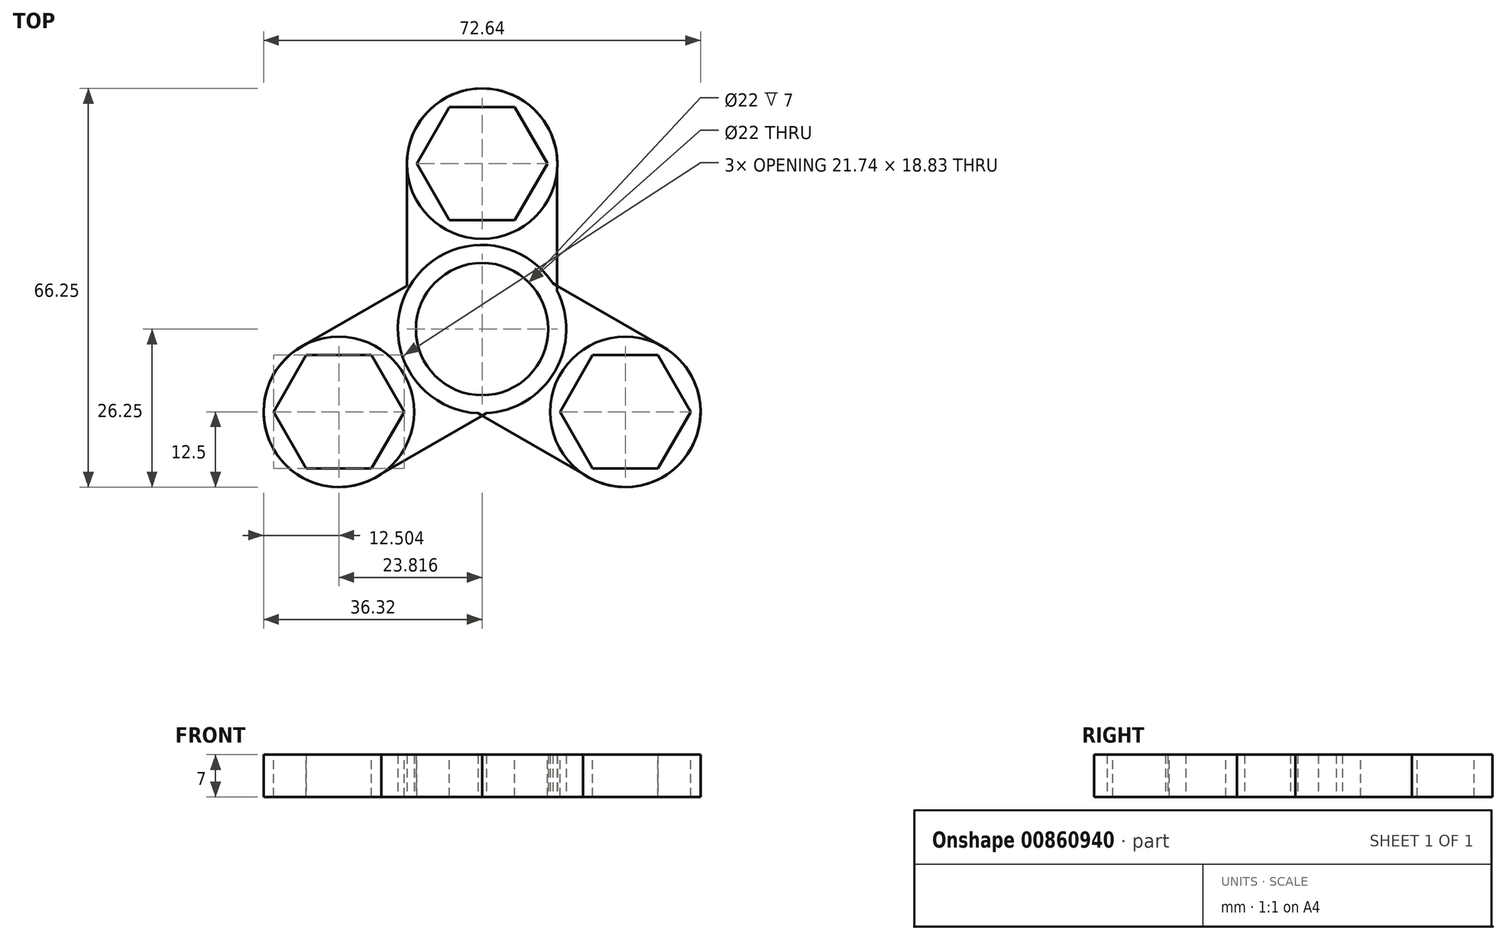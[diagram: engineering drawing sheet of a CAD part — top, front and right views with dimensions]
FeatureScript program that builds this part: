
annotation { "Feature Type Name" : "Feature", "Feature Type Description" : "" }
export const myFeature = defineFeature(function(context is Context, id is Id, definition is map)
    precondition{}
    {
        {
            var Q0;
            Q0=qCreatedBy(makeId("Top.planeOp"),FACE);
            var sketch = newSketch(context, id + "F0", { "sketchPlane" : qUnion([Q0])});
            skCircle(sketch, "E0", {"center": v(0, 0) * mm, "radius": 11 * mm});
            skCircle(sketch, "E1.0", {"center": v(0, 0) * mm, "radius": 14 * mm});
            skCircle(sketch, "E2", {"center": v(0, 0) * mm, "radius": 40 * mm, "construction": true});
            skCircle(sketch, "E3", {"center": v(0, 27.5) * mm, "radius": 12.5 * mm});
            skLineSegment(sketch, "E4", {"start": v(12.47, 26.57) * mm, "end": v(12.47, 6.37) * mm});
            skLineSegment(sketch, "E5", {"start": v(-12.47, 6.37) * mm, "end": v(-12.47, 26.57) * mm});
            skCircle(sketch, "E6.1.0", {"center": v(-23.82, -13.75) * mm, "radius": 12.5 * mm});
            skCircle(sketch, "E6.2.0", {"center": v(23.82, -13.75) * mm, "radius": 12.5 * mm});
            skLineSegment(sketch, "E7.1.0", {"start": v(0.71, -13.98) * mm, "end": v(-16.78, -24.08) * mm});
            skLineSegment(sketch, "E7.2.0", {"start": v(11.75, 7.6) * mm, "end": v(29.24, -2.49) * mm});
            skLineSegment(sketch, "E8.1.0", {"start": v(-29.24, -2.49) * mm, "end": v(-11.75, 7.6) * mm});
            skLineSegment(sketch, "E8.2.0", {"start": v(16.78, -24.08) * mm, "end": v(-0.71, -13.98) * mm});
            skSolve(sketch);
        }
        {
            var Q0;
            {var subQ0=sQuery(id+"F0.wireOp",EDGE,"E3");var subQ3=makeQuery(id+"F0.imprint","INTERSECT",VERTEX,{"derivedFrom":[subQ0,sQuery(id+"F0.wireOp",EDGE,"E4")]});Q0=makeQuery(id+"F0.imprint","IMPRINT",FACE,{"disambiguationData":[TD([[makeQuery(id+"F0.imprint","IMPRINT",EDGE,{"disambiguationData":[TD([[subQ3,-1.0]])],"derivedFrom":subQ0}),1.0]])]});}
            var Q1;
            {var subQ1=sQuery(id+"F0.wireOp",EDGE,"E1.0");var subQ9=sQuery(id+"F0.wireOp",EDGE,"E4");var subQ10=makeQuery(id+"F0.imprint","INTERSECT",VERTEX,{"derivedFrom":[subQ1,subQ9]});Q1=makeQuery(id+"F0.imprint","IMPRINT",FACE,{"disambiguationData":[TD([[makeQuery(id+"F0.imprint","IMPRINT",EDGE,{"disambiguationData":[TD([[subQ10,1.0]])],"derivedFrom":subQ1}),-1.0]])]});}
            var Q2;
            {var subQ2=sQuery(id+"F0.wireOp",EDGE,"076da4eb-b504-4ec3-a80a-fbc71ffce5cf.1.0");Q2=makeQuery(id+"F0.imprint","IMPRINT",FACE,{"disambiguationData":[TD([[makeQuery(id+"F0.imprint","IMPRINT",EDGE,{"derivedFrom":subQ2}),-1.0]])]});}
            var Q3;
            {var subQ0=sQuery(id+"F0.wireOp",EDGE,"E6.1.0");var subQ3=makeQuery(id+"F0.imprint","INTERSECT",VERTEX,{"derivedFrom":[subQ0,sQuery(id+"F0.wireOp",EDGE,"E8.1.0")]});Q3=makeQuery(id+"F0.imprint","IMPRINT",FACE,{"disambiguationData":[TD([[makeQuery(id+"F0.imprint","IMPRINT",EDGE,{"disambiguationData":[TD([[subQ3,-1.0]])],"derivedFrom":subQ0}),1.0]])]});}
            var Q4;
            {var subQ0=sQuery(id+"F0.wireOp",EDGE,"E6.2.0");var subQ3=makeQuery(id+"F0.imprint","INTERSECT",VERTEX,{"derivedFrom":[subQ0,sQuery(id+"F0.wireOp",EDGE,"E8.2.0")]});Q4=makeQuery(id+"F0.imprint","IMPRINT",FACE,{"disambiguationData":[TD([[makeQuery(id+"F0.imprint","IMPRINT",EDGE,{"disambiguationData":[TD([[subQ3,-1.0]])],"derivedFrom":subQ0}),1.0]])]});}
            var Q5;
            {var subQ7=sQuery(id+"F0.wireOp",EDGE,"E5");var subQ8=sQuery(id+"F0.wireOp",EDGE,"E1.0");var subQ9=makeQuery(id+"F0.imprint","INTERSECT",VERTEX,{"derivedFrom":[subQ8,subQ7]});Q5=makeQuery(id+"F0.imprint","IMPRINT",FACE,{"disambiguationData":[TD([[makeQuery(id+"F0.imprint","IMPRINT",EDGE,{"disambiguationData":[TD([[subQ9,-1.0]])],"derivedFrom":subQ8}),-1.0]])]});}
            var Q6;
            {var subQ2=sQuery(id+"F0.wireOp",EDGE,"076da4eb-b504-4ec3-a80a-fbc71ffce5cf.2.0");Q6=makeQuery(id+"F0.imprint","IMPRINT",FACE,{"disambiguationData":[TD([[makeQuery(id+"F0.imprint","IMPRINT",EDGE,{"derivedFrom":subQ2}),-1.0]])]});}
            var Q7;
            {var subQ0=sQuery(id+"F0.wireOp",EDGE,"wREQEkFX-s8tp-Np9Q-zugn-GrcXzJPVNxCA");Q7=makeQuery(id+"F0.imprint","IMPRINT",FACE,{"disambiguationData":[TD([[makeQuery(id+"F0.imprint","IMPRINT",EDGE,{"derivedFrom":subQ0}),-1.0]])]});}
            var Q8;
            Q8=makeQuery(id+"F0.imprint","IMPRINT",FACE,{"disambiguationData":[TD([[makeQuery(id+"F0.imprint","IMPRINT",EDGE,{"derivedFrom":sQuery(id+"F0.wireOp",EDGE,"E0")}),-1.0]])]});
            var Q9;
            {var subQ3=sQuery(id+"F0.wireOp",EDGE,"E7.2.0");var subQ9=sQuery(id+"F0.wireOp",EDGE,"E1.0");var subQ10=makeQuery(id+"F0.imprint","INTERSECT",VERTEX,{"derivedFrom":[subQ9,subQ3]});Q9=makeQuery(id+"F0.imprint","IMPRINT",FACE,{"disambiguationData":[TD([[makeQuery(id+"F0.imprint","IMPRINT",EDGE,{"disambiguationData":[TD([[subQ10,-1.0]])],"derivedFrom":subQ9}),-1.0]])]});}
            var Q10;
            {var subQ0=sQuery(id+"F0.wireOp",EDGE,"E5");var subQ1=sQuery(id+"F0.wireOp",EDGE,"E1.0");var subQ2=makeQuery(id+"F0.imprint","INTERSECT",VERTEX,{"derivedFrom":[subQ1,subQ0]});Q10=makeQuery(id+"F0.imprint","IMPRINT",FACE,{"disambiguationData":[TD([[makeQuery(id+"F0.imprint","IMPRINT",EDGE,{"disambiguationData":[TD([[subQ2,1.0]])],"derivedFrom":subQ1}),-1.0]])]});}
            var Q11;
            {var subQ0=sQuery(id+"F0.wireOp",EDGE,"E7.1.0");var subQ1=sQuery(id+"F0.wireOp",EDGE,"E1.0");var subQ2=makeQuery(id+"F0.imprint","INTERSECT",VERTEX,{"derivedFrom":[subQ1,subQ0]});Q11=makeQuery(id+"F0.imprint","IMPRINT",FACE,{"disambiguationData":[TD([[makeQuery(id+"F0.imprint","IMPRINT",EDGE,{"disambiguationData":[TD([[subQ2,1.0]])],"derivedFrom":subQ1}),-1.0]])]});}
            var Q12;
            {var subQ0=sQuery(id+"F0.wireOp",EDGE,"E4");var subQ1=sQuery(id+"F0.wireOp",EDGE,"E1.0");var subQ2=makeQuery(id+"F0.imprint","INTERSECT",VERTEX,{"derivedFrom":[subQ1,subQ0]});Q12=makeQuery(id+"F0.imprint","IMPRINT",FACE,{"disambiguationData":[TD([[makeQuery(id+"F0.imprint","IMPRINT",EDGE,{"disambiguationData":[TD([[subQ2,-1.0]])],"derivedFrom":subQ1}),-1.0]])]});}
            extrude(context, id + "F1", {"entities" : qUnion([Q0, Q1, Q2, Q3, Q4, Q5, Q6, Q7, Q8, Q9, Q10, Q11, Q12]), "depth" : 7 * mm, "offsetDistance" : 25 * mm});
        }
        {
            var Q0;
            Q0=makeQuery(id+"F1.opExtrude","CAP_FACE",FACE,{"disambiguationData":[OSD([sQuery(id+"F0.wireOp",EDGE,"E0"),sQuery(id+"F0.wireOp",EDGE,"E3"),sQuery(id+"F0.wireOp",EDGE,"E4"),sQuery(id+"F0.wireOp",EDGE,"E5"),sQuery(id+"F0.wireOp",EDGE,"E6.1.0"),sQuery(id+"F0.wireOp",EDGE,"E6.2.0"),sQuery(id+"F0.wireOp",EDGE,"E7.1.0"),sQuery(id+"F0.wireOp",EDGE,"E7.2.0"),sQuery(id+"F0.wireOp",EDGE,"E8.1.0"),sQuery(id+"F0.wireOp",EDGE,"E8.2.0"),sQuery(id+"F0.wireOp",EDGE,"wREQEkFX-s8tp-Np9Q-zugn-GrcXzJPVNxCA"),sQuery(id+"F0.wireOp",EDGE,"oM1CORSK-JYN6-xwzb-I89F-mR713MJxRMeX"),sQuery(id+"F0.wireOp",EDGE,"076da4eb-b504-4ec3-a80a-fbc71ffce5cf.1.0"),sQuery(id+"F0.wireOp",EDGE,"076da4eb-b504-4ec3-a80a-fbc71ffce5cf.2.0"),sQuery(id+"F0.wireOp",EDGE,"7e3cbf8b-2a53-4d2a-baa9-6ec39e642b55.1.0"),sQuery(id+"F0.wireOp",EDGE,"7e3cbf8b-2a53-4d2a-baa9-6ec39e642b55.2.0")])],"isStart":false});
            var sketch = newSketch(context, id + "F2", { "sketchPlane" : qUnion([Q0])});
            skCircle(sketch, "E9.cCircle", {"center": v(0, 27.5) * mm, "radius": 9.41 * mm, "construction": true});
            skLineSegment(sketch, "E9.0", {"start": v(-5.44, 36.92) * mm, "end": v(5.44, 36.92) * mm});
            skLineSegment(sketch, "E9.1", {"start": v(5.44, 36.92) * mm, "end": v(10.87, 27.5) * mm});
            skLineSegment(sketch, "E9.2", {"start": v(10.87, 27.5) * mm, "end": v(5.44, 18.09) * mm});
            skLineSegment(sketch, "E9.3", {"start": v(5.44, 18.09) * mm, "end": v(-5.44, 18.09) * mm});
            skLineSegment(sketch, "E9.4", {"start": v(-5.44, 18.09) * mm, "end": v(-10.87, 27.5) * mm});
            skLineSegment(sketch, "E9.5", {"start": v(-10.87, 27.5) * mm, "end": v(-5.44, 36.92) * mm});
            skPoint(sketch, "E9.0.midPoint", {"position": v(0, 36.92) * mm});
            skLineSegment(sketch, "E10.1.0", {"start": v(-12.94, -13.75) * mm, "end": v(-18.38, -23.16) * mm});
            skLineSegment(sketch, "E10.1.1", {"start": v(-18.38, -4.33) * mm, "end": v(-12.94, -13.75) * mm});
            skLineSegment(sketch, "E10.1.2", {"start": v(-29.25, -4.33) * mm, "end": v(-18.38, -4.33) * mm});
            skLineSegment(sketch, "E10.1.3", {"start": v(-34.69, -13.75) * mm, "end": v(-29.25, -4.33) * mm});
            skLineSegment(sketch, "E10.1.4", {"start": v(-18.38, -23.16) * mm, "end": v(-29.25, -23.16) * mm});
            skLineSegment(sketch, "E10.1.5", {"start": v(-29.25, -23.16) * mm, "end": v(-34.69, -13.75) * mm});
            skLineSegment(sketch, "E10.2.0", {"start": v(18.38, -4.34) * mm, "end": v(29.25, -4.34) * mm});
            skLineSegment(sketch, "E10.2.1", {"start": v(12.94, -13.75) * mm, "end": v(18.38, -4.34) * mm});
            skLineSegment(sketch, "E10.2.2", {"start": v(18.38, -23.17) * mm, "end": v(12.94, -13.75) * mm});
            skLineSegment(sketch, "E10.2.3", {"start": v(29.25, -23.17) * mm, "end": v(18.38, -23.17) * mm});
            skLineSegment(sketch, "E10.2.4", {"start": v(29.25, -4.34) * mm, "end": v(34.69, -13.75) * mm});
            skLineSegment(sketch, "E10.2.5", {"start": v(34.69, -13.75) * mm, "end": v(29.25, -23.17) * mm});
            skPoint(sketch, "E10.center", {"position": v(0, 0) * mm});
            skSolve(sketch);
        }
        {
            var Q0;
            Q0=makeQuery(id+"F2.imprint","IMPRINT",FACE,{"disambiguationData":[TD([[makeQuery(id+"F2.imprint","IMPRINT",EDGE,{"derivedFrom":sQuery(id+"F2.wireOp",EDGE,"E9.0")}),-1.0]])]});
            var Q1;
            Q1=makeQuery(id+"F2.imprint","IMPRINT",FACE,{"disambiguationData":[TD([[makeQuery(id+"F2.imprint","IMPRINT",EDGE,{"derivedFrom":sQuery(id+"F2.wireOp",EDGE,"E10.1.0")}),-1.0]])]});
            var Q2;
            Q2=makeQuery(id+"F2.imprint","IMPRINT",FACE,{"disambiguationData":[TD([[makeQuery(id+"F2.imprint","IMPRINT",EDGE,{"derivedFrom":sQuery(id+"F2.wireOp",EDGE,"E10.2.0")}),-1.0]])]});
            extrude(context, id + "F3", {"entities" : qUnion([Q0, Q1, Q2]), "operationType" : NewBodyOperationType.REMOVE, "oppositeDirection" : true, "depth" : 25 * mm, "offsetDistance" : 25 * mm});
        }
        {
            var Q0;
            {var subQ2=sQuery(id+"F0.wireOp",EDGE,"076da4eb-b504-4ec3-a80a-fbc71ffce5cf.2.0");Q0=makeQuery(id+"F0.imprint","IMPRINT",FACE,{"disambiguationData":[TD([[makeQuery(id+"F0.imprint","IMPRINT",EDGE,{"derivedFrom":subQ2}),-1.0]])]});}
            var Q1;
            {var subQ0=sQuery(id+"F0.wireOp",EDGE,"E6.1.0");var subQ3=makeQuery(id+"F0.imprint","INTERSECT",VERTEX,{"derivedFrom":[subQ0,sQuery(id+"F0.wireOp",EDGE,"E8.1.0")]});Q1=makeQuery(id+"F0.imprint","IMPRINT",FACE,{"disambiguationData":[TD([[makeQuery(id+"F0.imprint","IMPRINT",EDGE,{"disambiguationData":[TD([[subQ3,-1.0]])],"derivedFrom":subQ0}),1.0]])]});}
            var Q2;
            {var subQ0=sQuery(id+"F0.wireOp",EDGE,"E3");var subQ3=makeQuery(id+"F0.imprint","INTERSECT",VERTEX,{"derivedFrom":[subQ0,sQuery(id+"F0.wireOp",EDGE,"E4")]});Q2=makeQuery(id+"F0.imprint","IMPRINT",FACE,{"disambiguationData":[TD([[makeQuery(id+"F0.imprint","IMPRINT",EDGE,{"disambiguationData":[TD([[subQ3,-1.0]])],"derivedFrom":subQ0}),1.0]])]});}
            var Q3;
            {var subQ0=sQuery(id+"F0.wireOp",EDGE,"E6.2.0");var subQ3=makeQuery(id+"F0.imprint","INTERSECT",VERTEX,{"derivedFrom":[subQ0,sQuery(id+"F0.wireOp",EDGE,"E8.2.0")]});Q3=makeQuery(id+"F0.imprint","IMPRINT",FACE,{"disambiguationData":[TD([[makeQuery(id+"F0.imprint","IMPRINT",EDGE,{"disambiguationData":[TD([[subQ3,-1.0]])],"derivedFrom":subQ0}),1.0]])]});}
            var Q4;
            Q4=makeQuery(id+"F0.imprint","IMPRINT",FACE,{"disambiguationData":[TD([[makeQuery(id+"F0.imprint","IMPRINT",EDGE,{"derivedFrom":sQuery(id+"F0.wireOp",EDGE,"E0")}),-1.0]])]});
            var Q5;
            {var subQ0=sQuery(id+"F0.wireOp",EDGE,"E4");Q5=makeQuery(id+"F0.imprint","IMPRINT",FACE,{"disambiguationData":[TD([[makeQuery(id+"F0.imprint","IMPRINT",EDGE,{"derivedFrom":subQ0}),-1.0]])]});}
            var Q6;
            {var subQ0=sQuery(id+"F0.wireOp",EDGE,"E7.1.0");Q6=makeQuery(id+"F0.imprint","IMPRINT",FACE,{"disambiguationData":[TD([[makeQuery(id+"F0.imprint","IMPRINT",EDGE,{"derivedFrom":subQ0}),-1.0]])]});}
            var Q7;
            {var subQ2=sQuery(id+"F0.wireOp",EDGE,"076da4eb-b504-4ec3-a80a-fbc71ffce5cf.1.0");Q7=makeQuery(id+"F0.imprint","IMPRINT",FACE,{"disambiguationData":[TD([[makeQuery(id+"F0.imprint","IMPRINT",EDGE,{"derivedFrom":subQ2}),-1.0]])]});}
            var Q8;
            {var subQ0=sQuery(id+"F0.wireOp",EDGE,"wREQEkFX-s8tp-Np9Q-zugn-GrcXzJPVNxCA");Q8=makeQuery(id+"F0.imprint","IMPRINT",FACE,{"disambiguationData":[TD([[makeQuery(id+"F0.imprint","IMPRINT",EDGE,{"derivedFrom":subQ0}),-1.0]])]});}
            var Q9;
            {var subQ0=sQuery(id+"F0.wireOp",EDGE,"E7.2.0");Q9=makeQuery(id+"F0.imprint","IMPRINT",FACE,{"disambiguationData":[TD([[makeQuery(id+"F0.imprint","IMPRINT",EDGE,{"derivedFrom":subQ0}),-1.0]])]});}
            extrude(context, id + "F4", {"entities" : qUnion([Q0, Q1, Q2, Q3, Q4, Q5, Q6, Q7, Q8, Q9]), "depth" : 7 * mm, "offsetDistance" : 25 * mm});
        }
    });
